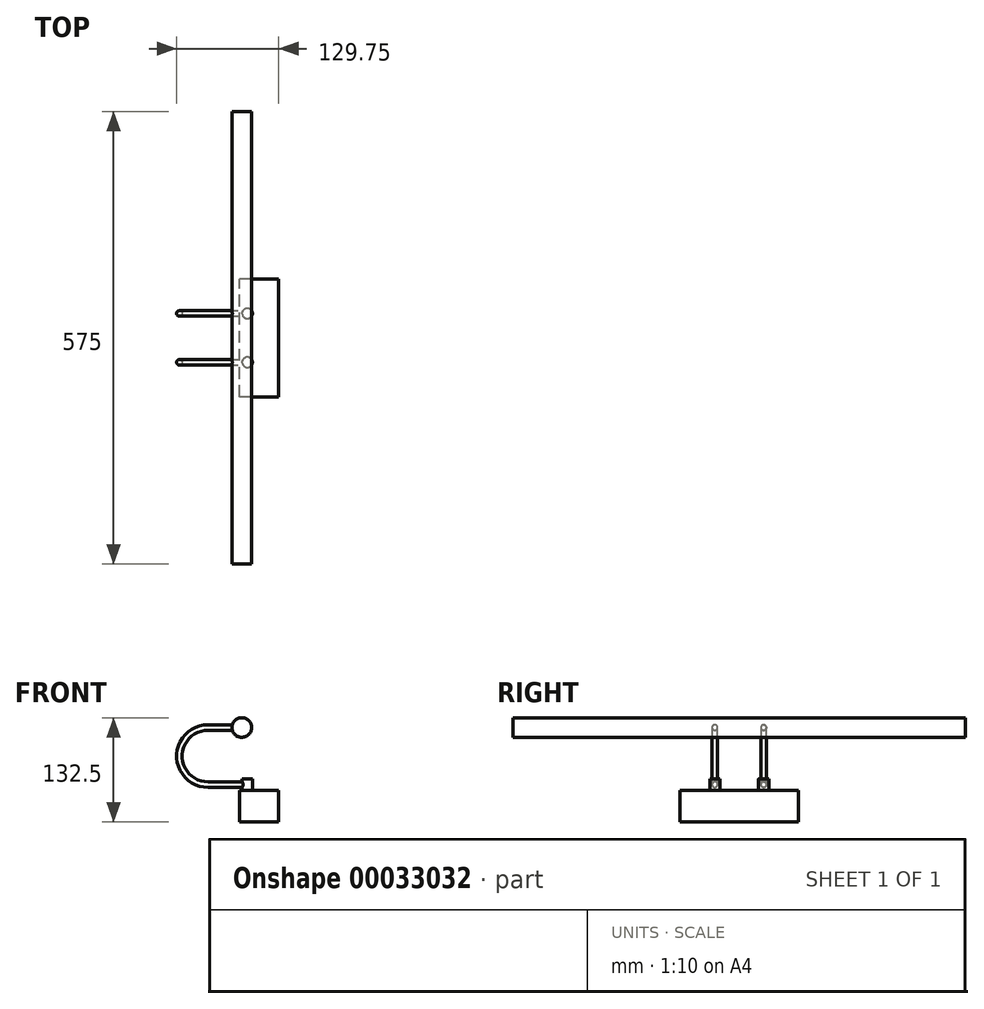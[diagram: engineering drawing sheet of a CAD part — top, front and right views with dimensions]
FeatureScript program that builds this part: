
annotation { "Feature Type Name" : "Feature", "Feature Type Description" : "" }
export const myFeature = defineFeature(function(context is Context, id is Id, definition is map)
    precondition{}
    {
        {
            var Q0;
            Q0=qCreatedBy(makeId("Top.planeOp"),FACE);
            var sketch = newSketch(context, id + "F0", { "sketchPlane" : qUnion([Q0])});
            skLineSegment(sketch, "E0.bottom", {"start": v(0, -75) * mm, "end": v(-50, -75) * mm});
            skLineSegment(sketch, "E0.top", {"start": v(0, 75) * mm, "end": v(-50, 75) * mm});
            skLineSegment(sketch, "E0.left", {"start": v(0, -75) * mm, "end": v(0, 75) * mm});
            skLineSegment(sketch, "E0.right", {"start": v(-50, -75) * mm, "end": v(-50, 75) * mm});
            skSolve(sketch);
        }
        {
            var Q0;
            Q0 = qSketchRegion(id + "F0", true);
            extrude(context, id + "F1", {"entities" : qUnion([Q0]), "depth" : 40 * mm});
        }
        {
            var Q0;
            Q0=makeQuery(id+"F1.opExtrude","CAP_FACE",FACE,{"disambiguationData":[OSD([sQuery(id+"F0.wireOp",EDGE,"E0.bottom"),sQuery(id+"F0.wireOp",EDGE,"E0.top"),sQuery(id+"F0.wireOp",EDGE,"E0.left"),sQuery(id+"F0.wireOp",EDGE,"E0.right")])],"isStart":false});
            var sketch = newSketch(context, id + "F2", { "sketchPlane" : qUnion([Q0])});
            skLineSegment(sketch, "E1", {"start": v(-40, -31) * mm, "end": v(-40, 31) * mm, "construction": true});
            skLineSegment(sketch, "E2", {"start": v(-40, 0) * mm, "end": v(-50, 0) * mm, "construction": true});
            skCircle(sketch, "E3", {"center": v(-40, -31) * mm, "radius": 6.5 * mm});
            skCircle(sketch, "E4", {"center": v(-40, 31) * mm, "radius": 6.5 * mm});
            skSolve(sketch);
        }
        {
            var Q0;
            Q0 = qSketchRegion(id + "F2", true);
            extrude(context, id + "F3", {"entities" : qUnion([Q0]), "operationType" : NewBodyOperationType.ADD, "depth" : 15 * mm});
        }
        {
            var Q0;
            Q0=qCreatedBy(makeId("Front.planeOp"),FACE);
            var sketch = newSketch(context, id + "F4", { "sketchPlane" : qUnion([Q0])});
            skCircle(sketch, "E5", {"center": v(-47, 120) * mm, "radius": 12.5 * mm});
            skSolve(sketch);
        }
        {
            var Q0;
            Q0 = qSketchRegion(id + "F4", true);
            extrude(context, id + "F5", {"entities" : qUnion([Q0]), "endBound" : BoundingType.SYMMETRIC, "depth" : 575 * mm});
        }
        {
            var Q0;
            Q0=qCreatedBy(makeId("Front.planeOp"),FACE);
            cPlane(context, id + "F6", {"entities" : qUnion([Q0]), "cplaneType" : CPlaneType.OFFSET, "offset" : (62 / 2) * mm, "width" : 150 * mm, "height" : 150 * mm});
        }
        {
            var Q0;
            Q0=qCreatedBy(id+"F6.planeOp",FACE);
            var sketch = newSketch(context, id + "F7", { "sketchPlane" : qUnion([Q0])});
            skLineSegment(sketch, "E6", {"start": v(-50, 120) * mm, "end": v(-90, 120) * mm});
            skLineSegment(sketch, "E7", {"start": v(-90, 120) * mm, "end": v(-90, 47.5) * mm, "construction": true});
            skLineSegment(sketch, "E8", {"start": v(-90, 47.5) * mm, "end": v(-40, 47.5) * mm});
            skArc(sketch, "E9", {"start": v(-90, 120) * mm, "mid": v(-126.25, 83.75) * mm, "end": v(-90, 47.5) * mm});
            skSolve(sketch);
        }
        {
            var Q0;
            Q0=sQuery(id+"F7.wireOp",VERTEX,"E6.start");
            var Q1;
            Q1=sQuery(id+"F7.wireOp",EDGE,"E6");
            cPlane(context, id + "F8", {"entities" : qUnion([Q0, Q1]), "cplaneType" : CPlaneType.LINE_POINT, "offset" : 150 * mm, "width" : 150 * mm, "height" : 150 * mm});
        }
        {
            var Q0;
            Q0=qCreatedBy(id+"F8.planeOp",FACE);
            var sketch = newSketch(context, id + "F9", { "sketchPlane" : qUnion([Q0])});
            skCircle(sketch, "E10", {"center": v(31, 120) * mm, "radius": 3.5 * mm});
            skSolve(sketch);
        }
        {
            var Q0;
            Q0 = qSketchRegion(id + "F9", true);
            var Q1;
            Q1 = qConstructionFilter(qBodyType(qCreatedBy(id + "F7" ,EDGE), BodyType.WIRE), ConstructionObject.NO);
            sweep(context, id + "F10", {"operationType" : NewBodyOperationType.ADD, "profiles" : qUnion([Q0]), "path" : qUnion([Q1])});
        }
        {
            var Q0;
            Q0=makeQuery(id+"F1.opExtrude","SWEPT_BODY",BODY,{"disambiguationData":[OSD([sQuery(id+"F0.wireOp",EDGE,"E0.bottom"),sQuery(id+"F0.wireOp",EDGE,"E0.top"),sQuery(id+"F0.wireOp",EDGE,"E0.left"),sQuery(id+"F0.wireOp",EDGE,"E0.right")])]});
            var Q1;
            Q1=qCreatedBy(makeId("Front.planeOp"),FACE);
            mirror(context, id + "F11", {"operationType" : NewBodyOperationType.ADD, "entities" : qUnion([Q0]), "mirrorPlane" : qUnion([Q1])});
        }
    });
